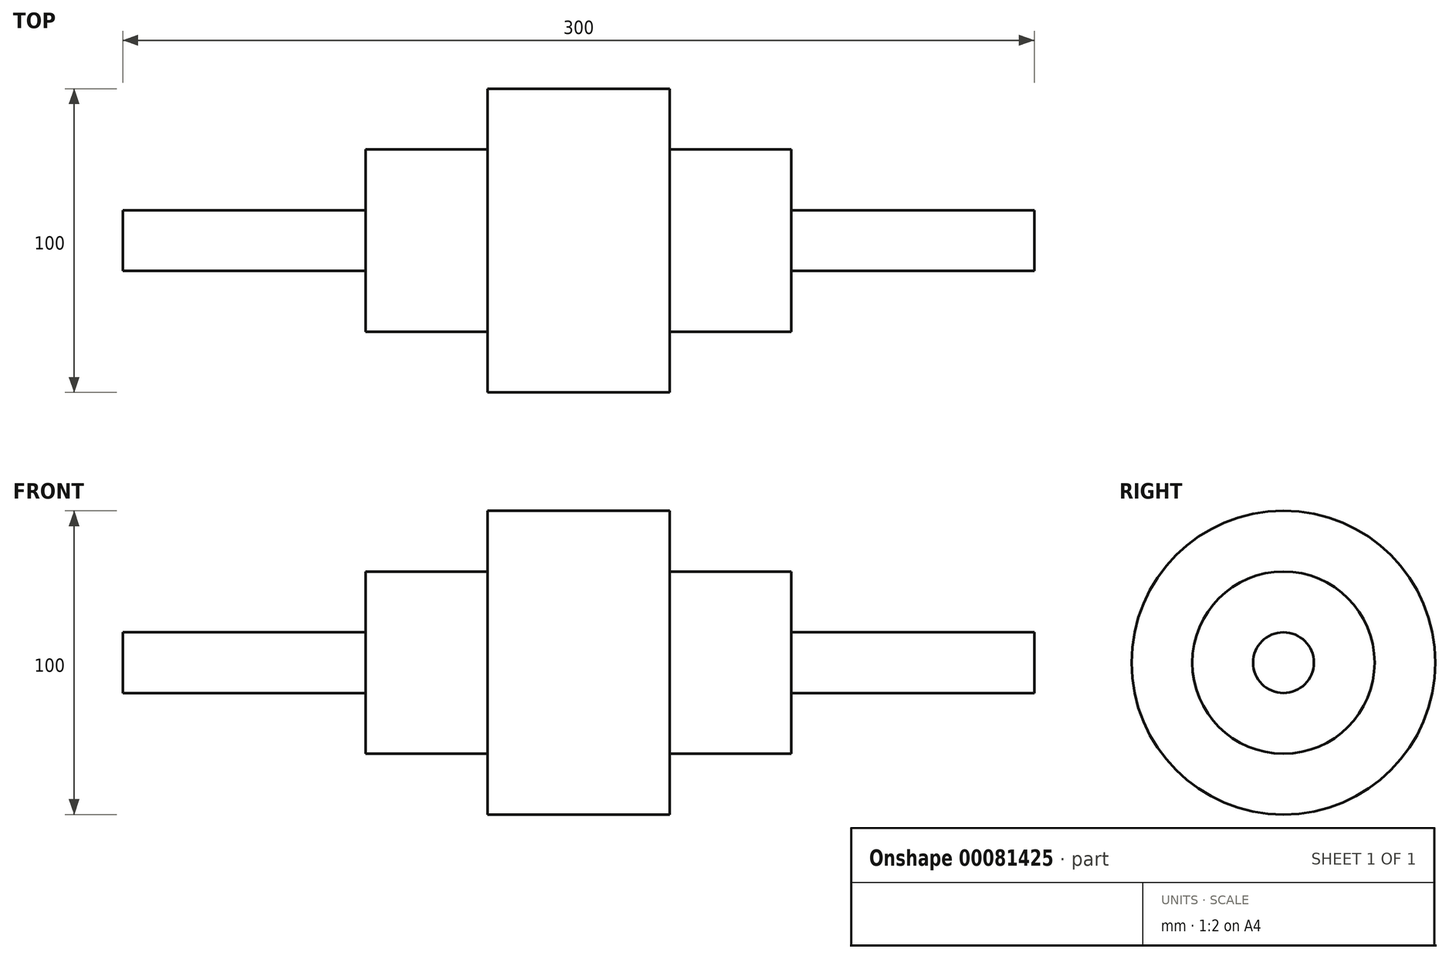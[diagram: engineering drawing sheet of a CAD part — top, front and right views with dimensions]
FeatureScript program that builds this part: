
annotation { "Feature Type Name" : "Feature", "Feature Type Description" : "" }
export const myFeature = defineFeature(function(context is Context, id is Id, definition is map)
    precondition{}
    {
        {
            var Q0;
            Q0=qCreatedBy(makeId("Front.planeOp"),FACE);
            var sketch = newSketch(context, id + "F0", { "sketchPlane" : qUnion([Q0])});
            skLineSegment(sketch, "E0", {"start": v(0, -31.54) * mm, "end": v(0, 38.62) * mm, "construction": true});
            skLineSegment(sketch, "E1", {"start": v(126.77, 0) * mm, "end": v(-144, 0) * mm, "construction": true});
            skLineSegment(sketch, "E2", {"start": v(-150, 0) * mm, "end": v(-150, 10) * mm});
            skLineSegment(sketch, "E3", {"start": v(-150, 10) * mm, "end": v(-70, 10) * mm});
            skLineSegment(sketch, "E4", {"start": v(-70, 10) * mm, "end": v(-70, 0) * mm});
            skLineSegment(sketch, "E5", {"start": v(-70, 0) * mm, "end": v(-70, 30) * mm});
            skLineSegment(sketch, "E6", {"start": v(-70, 30) * mm, "end": v(-30, 30) * mm});
            skLineSegment(sketch, "E7", {"start": v(-30, 30) * mm, "end": v(-30, 0) * mm});
            skLineSegment(sketch, "E8", {"start": v(-30, 0) * mm, "end": v(-30, 50) * mm});
            skLineSegment(sketch, "E9", {"start": v(-30, 50) * mm, "end": v(0, 50) * mm});
            skLineSegment(sketch, "E10", {"start": v(0, 50) * mm, "end": v(0, 0) * mm});
            skLineSegment(sketch, "E11", {"start": v(0, 0) * mm, "end": v(-150, 0) * mm});
            skLineSegment(sketch, "E12.MirrorCS", {"start": v(30, 50) * mm, "end": v(0, 50) * mm});
            skLineSegment(sketch, "E13.MirrorCS", {"start": v(30, 0) * mm, "end": v(30, 50) * mm});
            skLineSegment(sketch, "E14.MirrorCS", {"start": v(70, 30) * mm, "end": v(30, 30) * mm});
            skLineSegment(sketch, "E15.MirrorCS", {"start": v(70, 0) * mm, "end": v(70, 30) * mm});
            skLineSegment(sketch, "E16.MirrorCS", {"start": v(150, 10) * mm, "end": v(70, 10) * mm});
            skLineSegment(sketch, "E17.MirrorCS", {"start": v(150, 0) * mm, "end": v(150, 10) * mm});
            skLineSegment(sketch, "E18.MirrorCS", {"start": v(150, 0) * mm, "end": v(150, -10) * mm});
            skLineSegment(sketch, "E19.MirrorCS", {"start": v(150, -10) * mm, "end": v(70, -10) * mm});
            skLineSegment(sketch, "E20.MirrorCS", {"start": v(70, 0) * mm, "end": v(70, -30) * mm});
            skLineSegment(sketch, "E21.MirrorCS", {"start": v(70, -30) * mm, "end": v(30, -30) * mm});
            skLineSegment(sketch, "E22.MirrorCS", {"start": v(30, 0) * mm, "end": v(30, -50) * mm});
            skLineSegment(sketch, "E23.MirrorCS", {"start": v(30, -50) * mm, "end": v(0, -50) * mm});
            skLineSegment(sketch, "E24.MirrorCS", {"start": v(-30, -50) * mm, "end": v(0, -50) * mm});
            skLineSegment(sketch, "E25.MirrorCS", {"start": v(-30, 0) * mm, "end": v(-30, -50) * mm});
            skLineSegment(sketch, "E26.MirrorCS", {"start": v(-70, -30) * mm, "end": v(-30, -30) * mm});
            skLineSegment(sketch, "E27.MirrorCS", {"start": v(-70, 0) * mm, "end": v(-70, -30) * mm});
            skLineSegment(sketch, "E28.MirrorCS", {"start": v(-150, -10) * mm, "end": v(-70, -10) * mm});
            skLineSegment(sketch, "E29.MirrorCS", {"start": v(-150, 0) * mm, "end": v(-150, -10) * mm});
            skLineSegment(sketch, "E30", {"start": v(-150, 0) * mm, "end": v(150, 0) * mm});
            skSolve(sketch);
        }
        {
            var Q0;
            {var subQ0=sQuery(id+"F0.wireOp",EDGE,"E18.MirrorCS");Q0=makeQuery(id+"F0.imprint","IMPRINT",FACE,{"disambiguationData":[TD([[makeQuery(id+"F0.imprint","IMPRINT",EDGE,{"derivedFrom":subQ0}),-1.0]])]});}
            var Q1;
            {var subQ3=sQuery(id+"F0.wireOp",EDGE,"E28.MirrorCS");Q1=makeQuery(id+"F0.imprint","IMPRINT",FACE,{"disambiguationData":[TD([[makeQuery(id+"F0.imprint","IMPRINT",EDGE,{"derivedFrom":subQ3}),1.0]])]});}
            var Q2;
            {var subQ3=sQuery(id+"F0.wireOp",EDGE,"E21.MirrorCS");Q2=makeQuery(id+"F0.imprint","IMPRINT",FACE,{"disambiguationData":[TD([[makeQuery(id+"F0.imprint","IMPRINT",EDGE,{"derivedFrom":subQ3}),-1.0]])]});}
            var Q3;
            {var subQ1=sQuery(id+"F0.wireOp",EDGE,"E26.MirrorCS");Q3=makeQuery(id+"F0.imprint","IMPRINT",FACE,{"disambiguationData":[TD([[makeQuery(id+"F0.imprint","IMPRINT",EDGE,{"derivedFrom":subQ1}),1.0]])]});}
            var Q4;
            {var subQ1=sQuery(id+"F0.wireOp",EDGE,"E23.MirrorCS");Q4=makeQuery(id+"F0.imprint","IMPRINT",FACE,{"disambiguationData":[TD([[makeQuery(id+"F0.imprint","IMPRINT",EDGE,{"derivedFrom":subQ1}),-1.0]])]});}
            var Q5;
            Q5=sQuery(id+"F0.wireOp",EDGE,"E30");
            revolve(context, id + "F1", {"entities" : qUnion([Q0, Q1, Q2, Q3, Q4]), "axis" : qUnion([Q5]), "revolveType" : RevolveType.FULL});
        }
    });
